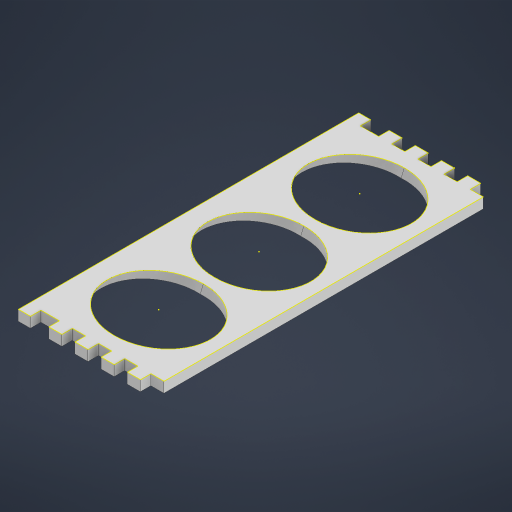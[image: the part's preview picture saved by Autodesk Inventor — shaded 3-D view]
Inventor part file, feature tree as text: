
AUTODESK INVENTOR PART (.ipt)
format: ipt  version: 2023 (Build 270158030, 158C)  size: 360,448 bytes
history: native  units: mm
features: sketch x4, extrude x3, plane x1, projected_geometry x1
ambient origin geometry x8: Origin, YZ Plane, XZ Plane, XY Plane, X Axis, Y Axis, Z Axis, Center Point
bodies: Solid1 (feature_tree)
feature tree (9):
  extrude  "Extrusion1"  TaperAngle=30.0deg  [1 undecoded]
  plane  "Work Plane1"
  extrude  "Extrusion2"  Depth=7.000109mm TaperAngle=0.0deg
  extrude  "Extrusion3"  [1 undecoded]
  sketch  "Sketch5"
  sketch  "Sketch1"  dims[d0=4.0mm d1=0.0mm d2=30.0deg]
  sketch  "Sketch3"  dims[d3=132.004478mm d4=172.003386mm d5=7.003386mm d6=3.880396mm d7=47.003386mm d8=125.0mm d9=5.0mm d10=7.000109mm d11=8.0mm d12=31.75mm d13=0.0mm]
  sketch  "Sketch4"  dims[d14=31.75mm d15=0.0mm]
  projected_geometry  "Projected Loop2"
note: 2 required parameter values undecoded (feature->parameter linkage not recoverable at this tier; creation-order binding heuristic only, values carry confidence <= 0.55)
